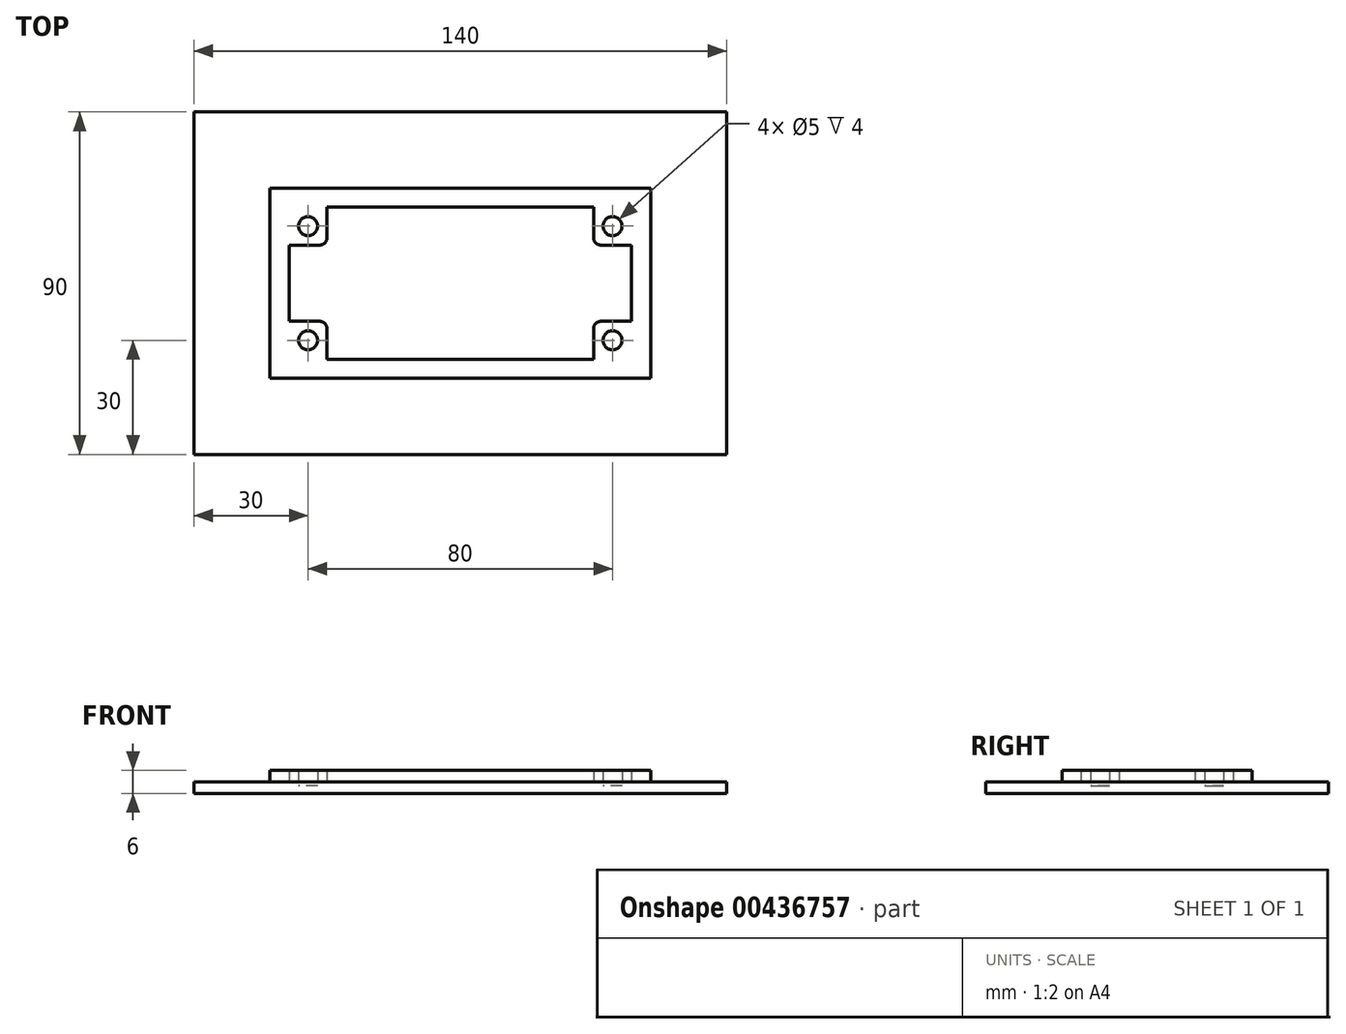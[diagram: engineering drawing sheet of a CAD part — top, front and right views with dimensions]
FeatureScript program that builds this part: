
annotation { "Feature Type Name" : "Feature", "Feature Type Description" : "" }
export const myFeature = defineFeature(function(context is Context, id is Id, definition is map)
    precondition{}
    {
        {
            var Q0;
            Q0=qCreatedBy(makeId("Top.planeOp"),FACE);
            var sketch = newSketch(context, id + "F0", { "sketchPlane" : qUnion([Q0])});
            skLineSegment(sketch, "E0.bottom", {"start": v(-50, 25) * mm, "end": v(50, 25) * mm});
            skLineSegment(sketch, "E0.top", {"start": v(-50, -25) * mm, "end": v(50, -25) * mm});
            skLineSegment(sketch, "E0.left", {"start": v(-50, 25) * mm, "end": v(-50, -25) * mm});
            skLineSegment(sketch, "E0.right", {"start": v(50, 25) * mm, "end": v(50, -25) * mm});
            skPoint(sketch, "E0.middle", {"position": v(0, 0) * mm});
            skLineSegment(sketch, "E1.0", {"start": v(-45, 20) * mm, "end": v(45, 20) * mm});
            skLineSegment(sketch, "E1.1", {"start": v(-45, 20) * mm, "end": v(-45, -20) * mm});
            skLineSegment(sketch, "E1.2", {"start": v(-45, -20) * mm, "end": v(45, -20) * mm});
            skLineSegment(sketch, "E1.3", {"start": v(45, 20) * mm, "end": v(45, -20) * mm});
            skLineSegment(sketch, "E2.0", {"start": v(-70, 45) * mm, "end": v(70, 45) * mm});
            skLineSegment(sketch, "E2.1", {"start": v(-70, 45) * mm, "end": v(-70, -45) * mm});
            skLineSegment(sketch, "E2.2", {"start": v(-70, -45) * mm, "end": v(70, -45) * mm});
            skLineSegment(sketch, "E2.3", {"start": v(70, 45) * mm, "end": v(70, -45) * mm});
            skLineSegment(sketch, "E3", {"start": v(-45, 10) * mm, "end": v(-35, 10) * mm});
            skLineSegment(sketch, "E4", {"start": v(-35, 10) * mm, "end": v(-35, 20) * mm});
            skLineSegment(sketch, "E5", {"start": v(35, 20) * mm, "end": v(35, 10) * mm});
            skLineSegment(sketch, "E6", {"start": v(35, 10) * mm, "end": v(45, 10) * mm});
            skLineSegment(sketch, "E7", {"start": v(-35, -20) * mm, "end": v(-35, -10) * mm});
            skLineSegment(sketch, "E8", {"start": v(-35, -10) * mm, "end": v(-45, -10) * mm});
            skLineSegment(sketch, "E9", {"start": v(45, -10) * mm, "end": v(35, -10) * mm});
            skLineSegment(sketch, "E10", {"start": v(35, -10) * mm, "end": v(35, -20) * mm});
            skPoint(sketch, "E11", {"position": v(-40, 15) * mm});
            skPoint(sketch, "E11.positionSnap0", {"position": v(-35, 15) * mm});
            skPoint(sketch, "E11.positionSnap1", {"position": v(-40, 10) * mm});
            skPoint(sketch, "E12", {"position": v(40, 15) * mm});
            skPoint(sketch, "E12.positionSnap0", {"position": v(40, 10) * mm});
            skPoint(sketch, "E12.positionSnap1", {"position": v(35, 15) * mm});
            skPoint(sketch, "E13", {"position": v(40, -15) * mm});
            skPoint(sketch, "E13.positionSnap0", {"position": v(35, -15) * mm});
            skPoint(sketch, "E13.positionSnap1", {"position": v(40, -10) * mm});
            skPoint(sketch, "E14", {"position": v(-40, -15) * mm});
            skPoint(sketch, "E14.positionSnap0", {"position": v(-35, -15) * mm});
            skPoint(sketch, "E14.positionSnap1", {"position": v(-40, -10) * mm});
            skCircle(sketch, "E15", {"center": v(-40, 15) * mm, "radius": 2.5 * mm});
            skCircle(sketch, "E16", {"center": v(40, 15) * mm, "radius": 2.5 * mm});
            skCircle(sketch, "E17", {"center": v(40, -15) * mm, "radius": 2.5 * mm});
            skCircle(sketch, "E18", {"center": v(-40, -15) * mm, "radius": 2.5 * mm});
            skSolve(sketch);
        }
        {
            var Q0;
            Q0=makeQuery(id+"F0.imprint","IMPRINT",FACE,{"disambiguationData":[TD([[makeQuery(id+"F0.imprint","IMPRINT",EDGE,{"derivedFrom":sQuery(id+"F0.wireOp",EDGE,"E0.bottom")}),-1.0]])]});
            extrude(context, id + "F1", {"entities" : qUnion([Q0]), "depth" : 6 * mm});
        }
        {
            var Q0;
            Q0=makeQuery(id+"F0.imprint","IMPRINT",FACE,{"disambiguationData":[TD([[makeQuery(id+"F0.imprint","IMPRINT",EDGE,{"derivedFrom":sQuery(id+"F0.wireOp",EDGE,"E0.bottom")}),1.0]])]});
            extrude(context, id + "F2", {"entities" : qUnion([Q0]), "operationType" : NewBodyOperationType.ADD, "depth" : 3 * mm});
        }
        {
            var Q0;
            Q0 = qSketchRegion(id + "F0", true);
            var Q1;
            {var subQ3=sQuery(id+"F0.wireOp",EDGE,"E3");Q1=makeQuery(id+"F0.imprint","IMPRINT",FACE,{"disambiguationData":[TD([[makeQuery(id+"F0.imprint","IMPRINT",EDGE,{"derivedFrom":subQ3}),-1.0]])]});}
            extrude(context, id + "F3", {"entities" : qUnion([Q0, Q1]), "operationType" : NewBodyOperationType.ADD, "depth" : 3 * mm});
        }
        {
            var Q0;
            {var subQ1=sQuery(id+"F0.wireOp",EDGE,"E3");Q0=makeQuery(id+"F0.imprint","IMPRINT",FACE,{"disambiguationData":[TD([[makeQuery(id+"F0.imprint","IMPRINT",EDGE,{"derivedFrom":subQ1}),1.0]])]});}
            var Q1;
            {var subQ0=sQuery(id+"F0.wireOp",EDGE,"E5");Q1=makeQuery(id+"F0.imprint","IMPRINT",FACE,{"disambiguationData":[TD([[makeQuery(id+"F0.imprint","IMPRINT",EDGE,{"derivedFrom":subQ0}),1.0]])]});}
            var Q2;
            {var subQ0=sQuery(id+"F0.wireOp",EDGE,"E9");Q2=makeQuery(id+"F0.imprint","IMPRINT",FACE,{"disambiguationData":[TD([[makeQuery(id+"F0.imprint","IMPRINT",EDGE,{"derivedFrom":subQ0}),1.0]])]});}
            var Q3;
            {var subQ4=sQuery(id+"F0.wireOp",EDGE,"E7");Q3=makeQuery(id+"F0.imprint","IMPRINT",FACE,{"disambiguationData":[TD([[makeQuery(id+"F0.imprint","IMPRINT",EDGE,{"derivedFrom":subQ4}),1.0]])]});}
            extrude(context, id + "F4", {"entities" : qUnion([Q0, Q1, Q2, Q3]), "operationType" : NewBodyOperationType.ADD, "depth" : 6 * mm});
        }
        {
            var Q0;
            Q0=makeQuery(id+"F0.imprint","IMPRINT",FACE,{"disambiguationData":[TD([[makeQuery(id+"F0.imprint","IMPRINT",EDGE,{"derivedFrom":sQuery(id+"F0.wireOp",EDGE,"E16")}),1.0]])]});
            var Q1;
            Q1=makeQuery(id+"F0.imprint","IMPRINT",FACE,{"disambiguationData":[TD([[makeQuery(id+"F0.imprint","IMPRINT",EDGE,{"derivedFrom":sQuery(id+"F0.wireOp",EDGE,"E15")}),1.0]])]});
            var Q2;
            Q2=makeQuery(id+"F0.imprint","IMPRINT",FACE,{"disambiguationData":[TD([[makeQuery(id+"F0.imprint","IMPRINT",EDGE,{"derivedFrom":sQuery(id+"F0.wireOp",EDGE,"E17")}),1.0]])]});
            var Q3;
            Q3=makeQuery(id+"F0.imprint","IMPRINT",FACE,{"disambiguationData":[TD([[makeQuery(id+"F0.imprint","IMPRINT",EDGE,{"derivedFrom":sQuery(id+"F0.wireOp",EDGE,"E18")}),1.0]])]});
            extrude(context, id + "F5", {"entities" : qUnion([Q0, Q1, Q2, Q3]), "operationType" : NewBodyOperationType.ADD, "depth" : 2 * mm});
        }
        {
            var Q0;
            Q0=makeQuery(id+"F4.opExtrude","SWEPT_EDGE",EDGE,{"disambiguationData":[OSD([sQuery(id+"F0.wireOp",EDGE,"E3"),sQuery(id+"F0.wireOp",EDGE,"E4")])]});
            var Q1;
            Q1=makeQuery(id+"F4.opExtrude","SWEPT_EDGE",EDGE,{"disambiguationData":[OSD([sQuery(id+"F0.wireOp",EDGE,"E5"),sQuery(id+"F0.wireOp",EDGE,"E6")])]});
            var Q2;
            Q2=makeQuery(id+"F4.opExtrude","SWEPT_EDGE",EDGE,{"disambiguationData":[OSD([sQuery(id+"F0.wireOp",EDGE,"E1.0"),sQuery(id+"F0.wireOp",EDGE,"E5")])]});
            var Q3;
            Q3=makeQuery(id+"F4.opExtrude","SWEPT_EDGE",EDGE,{"disambiguationData":[OSD([sQuery(id+"F0.wireOp",EDGE,"E1.3"),sQuery(id+"F0.wireOp",EDGE,"E6")])]});
            var Q4;
            Q4=makeQuery(id+"F4.opExtrude","SWEPT_EDGE",EDGE,{"disambiguationData":[OSD([sQuery(id+"F0.wireOp",EDGE,"E1.0"),sQuery(id+"F0.wireOp",EDGE,"E4")])]});
            var Q5;
            Q5=makeQuery(id+"F4.opExtrude","SWEPT_EDGE",EDGE,{"disambiguationData":[OSD([sQuery(id+"F0.wireOp",EDGE,"E1.1"),sQuery(id+"F0.wireOp",EDGE,"E3")])]});
            var Q6;
            Q6=makeQuery(id+"F4.opExtrude","SWEPT_EDGE",EDGE,{"disambiguationData":[OSD([sQuery(id+"F0.wireOp",EDGE,"E1.3"),sQuery(id+"F0.wireOp",EDGE,"E9")])]});
            var Q7;
            Q7=makeQuery(id+"F4.opExtrude","SWEPT_EDGE",EDGE,{"disambiguationData":[OSD([sQuery(id+"F0.wireOp",EDGE,"E9"),sQuery(id+"F0.wireOp",EDGE,"E10")])]});
            var Q8;
            Q8=makeQuery(id+"F4.opExtrude","SWEPT_EDGE",EDGE,{"disambiguationData":[OSD([sQuery(id+"F0.wireOp",EDGE,"E1.2"),sQuery(id+"F0.wireOp",EDGE,"E10")])]});
            var Q9;
            Q9=makeQuery(id+"F4.opExtrude","SWEPT_EDGE",EDGE,{"disambiguationData":[OSD([sQuery(id+"F0.wireOp",EDGE,"E1.1"),sQuery(id+"F0.wireOp",EDGE,"E8")])]});
            var Q10;
            Q10=makeQuery(id+"F4.opExtrude","SWEPT_EDGE",EDGE,{"disambiguationData":[OSD([sQuery(id+"F0.wireOp",EDGE,"E7"),sQuery(id+"F0.wireOp",EDGE,"E8")])]});
            var Q11;
            Q11=makeQuery(id+"F4.opExtrude","SWEPT_EDGE",EDGE,{"disambiguationData":[OSD([sQuery(id+"F0.wireOp",EDGE,"E1.2"),sQuery(id+"F0.wireOp",EDGE,"E7")])]});
            fillet(context, id + "F6", {"entities" : qUnion([Q0, Q1, Q2, Q3, Q4, Q5, Q6, Q7, Q8, Q9, Q10, Q11]), "radius" : 2 * mm, "tangentPropagation" : true, "allowEdgeOverflow" : false});
        }
    });
